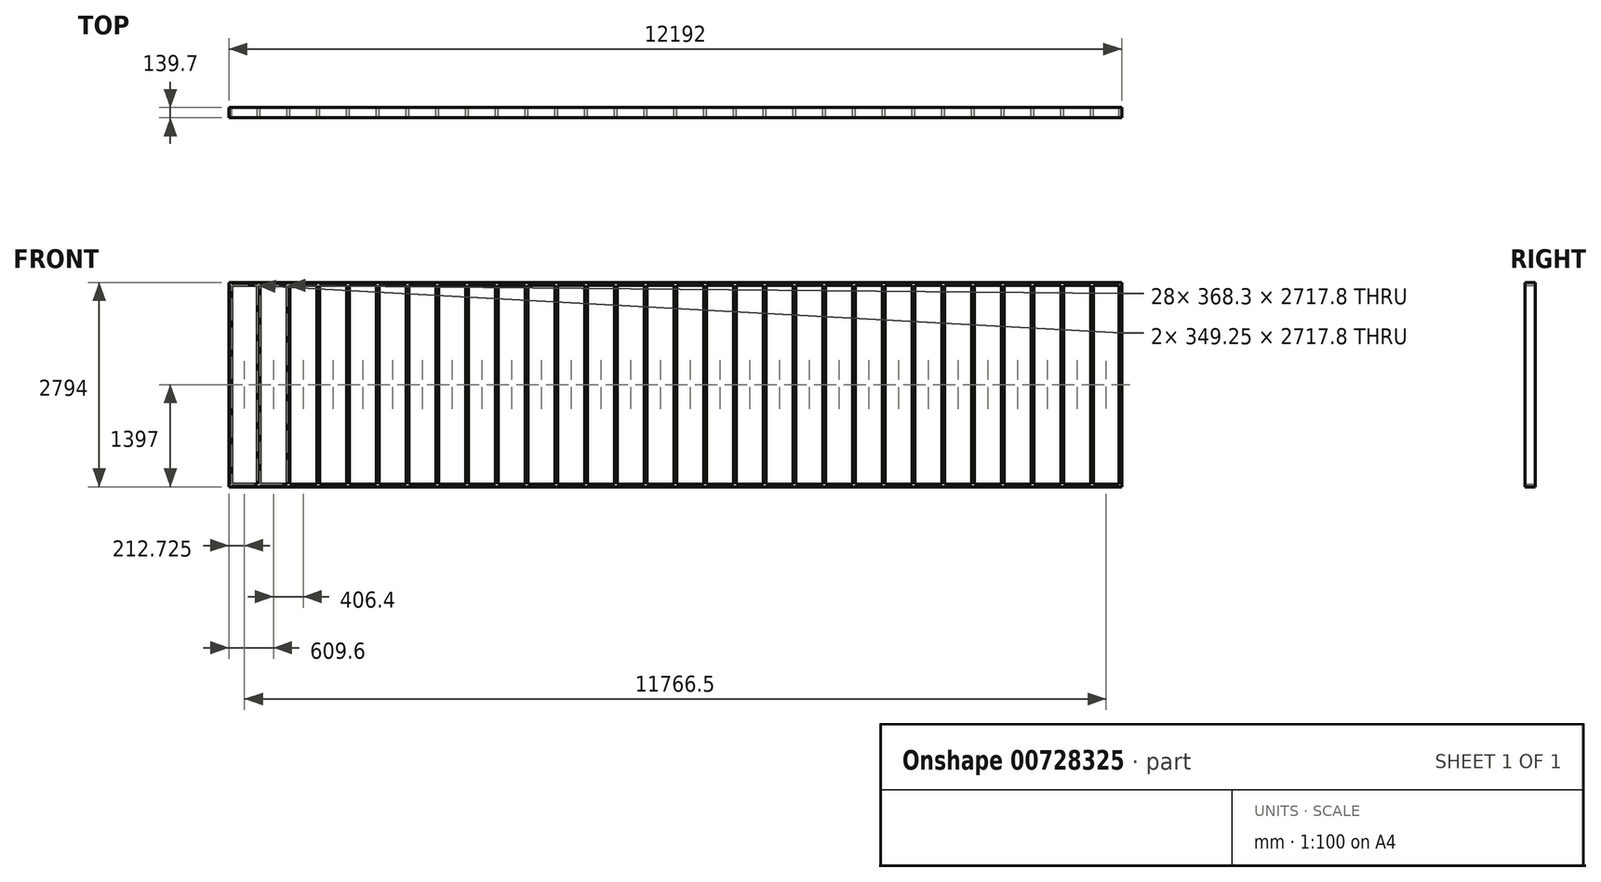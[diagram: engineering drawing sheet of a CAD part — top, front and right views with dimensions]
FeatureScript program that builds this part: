
annotation { "Feature Type Name" : "Feature", "Feature Type Description" : "" }
export const myFeature = defineFeature(function(context is Context, id is Id, definition is map)
    precondition{}
    {
        {
            var Q0;
            Q0=qCreatedBy(makeId("Front.planeOp"),FACE);
            var sketch = newSketch(context, id + "F0", { "sketchPlane" : qUnion([Q0])});
            skLineSegment(sketch, "E0.bottom", {"start": v(-6096, -1397) * mm, "end": v(6096, -1397) * mm});
            skLineSegment(sketch, "E0.top", {"start": v(-6096, 1397) * mm, "end": v(6096, 1397) * mm});
            skLineSegment(sketch, "E0.left", {"start": v(-6096, -1397) * mm, "end": v(-6096, 1397) * mm});
            skLineSegment(sketch, "E0.right", {"start": v(6096, -1397) * mm, "end": v(6096, 1397) * mm});
            skPoint(sketch, "E0.middle", {"position": v(0, 0) * mm});
            skLineSegment(sketch, "E1.0", {"start": v(-6057.9, -1358.9) * mm, "end": v(-6057.9, 1358.9) * mm});
            skLineSegment(sketch, "E2.0", {"start": v(-5708.65, -1358.9) * mm, "end": v(-5708.65, 1358.9) * mm});
            skLineSegment(sketch, "E3.0", {"start": v(-5670.55, -1358.9) * mm, "end": v(-5670.55, 1358.9) * mm});
            skLineSegment(sketch, "E4.0", {"start": v(-5302.25, -1358.9) * mm, "end": v(-5302.25, 1358.9) * mm});
            skLineSegment(sketch, "E5.0", {"start": v(-5264.15, -1358.9) * mm, "end": v(-5264.15, 1358.9) * mm});
            skLineSegment(sketch, "E6.0", {"start": v(-4895.85, -1358.9) * mm, "end": v(-4895.85, 1358.9) * mm});
            skLineSegment(sketch, "E7.0", {"start": v(-4857.75, -1358.9) * mm, "end": v(-4857.75, 1358.9) * mm});
            skLineSegment(sketch, "E8.0", {"start": v(-4489.45, -1358.9) * mm, "end": v(-4489.45, 1358.9) * mm});
            skLineSegment(sketch, "E9.0", {"start": v(-4451.35, -1358.9) * mm, "end": v(-4451.35, 1358.9) * mm});
            skLineSegment(sketch, "E10.0", {"start": v(-4083.05, -1358.9) * mm, "end": v(-4083.05, 1358.9) * mm});
            skLineSegment(sketch, "E11.0", {"start": v(-4044.95, -1358.9) * mm, "end": v(-4044.95, 1358.9) * mm});
            skLineSegment(sketch, "E12.0", {"start": v(-3676.65, -1358.9) * mm, "end": v(-3676.65, 1358.9) * mm});
            skLineSegment(sketch, "E13.0", {"start": v(-3638.55, -1358.9) * mm, "end": v(-3638.55, 1358.9) * mm});
            skLineSegment(sketch, "E14.0", {"start": v(-3270.25, -1358.9) * mm, "end": v(-3270.25, 1358.9) * mm});
            skLineSegment(sketch, "E15.0", {"start": v(-3232.15, -1358.9) * mm, "end": v(-3232.15, 1358.9) * mm});
            skLineSegment(sketch, "E16.0", {"start": v(-2863.85, -1397) * mm, "end": v(-2863.85, 1358.9) * mm});
            skLineSegment(sketch, "E17.0", {"start": v(-2825.75, -1397) * mm, "end": v(-2825.75, 1358.9) * mm});
            skLineSegment(sketch, "E18.0", {"start": v(-2457.45, -1358.9) * mm, "end": v(-2457.45, 1358.9) * mm});
            skLineSegment(sketch, "E19.0", {"start": v(-2419.35, -1358.9) * mm, "end": v(-2419.35, 1358.9) * mm});
            skLineSegment(sketch, "E20.0", {"start": v(-2051.05, -1358.9) * mm, "end": v(-2051.05, 1358.9) * mm});
            skLineSegment(sketch, "E21.0", {"start": v(-2012.95, -1358.9) * mm, "end": v(-2012.95, 1358.9) * mm});
            skLineSegment(sketch, "E22.0", {"start": v(-1644.65, -1358.9) * mm, "end": v(-1644.65, 1358.9) * mm});
            skLineSegment(sketch, "E23.0", {"start": v(-1606.55, -1358.9) * mm, "end": v(-1606.55, 1358.9) * mm});
            skLineSegment(sketch, "E24.0", {"start": v(-1238.25, -1358.9) * mm, "end": v(-1238.25, 1358.9) * mm});
            skLineSegment(sketch, "E25.0", {"start": v(-1200.15, -1358.9) * mm, "end": v(-1200.15, 1358.9) * mm});
            skLineSegment(sketch, "E26.0", {"start": v(-831.85, -1358.9) * mm, "end": v(-831.85, 1358.9) * mm});
            skLineSegment(sketch, "E27.0", {"start": v(-793.75, -1358.9) * mm, "end": v(-793.75, 1358.9) * mm});
            skLineSegment(sketch, "E28.0", {"start": v(-425.45, -1358.9) * mm, "end": v(-425.45, 1358.9) * mm});
            skLineSegment(sketch, "E29.0", {"start": v(-387.35, -1358.9) * mm, "end": v(-387.35, 1358.9) * mm});
            skLineSegment(sketch, "E30.0", {"start": v(-19.05, -1358.9) * mm, "end": v(-19.05, 1358.9) * mm});
            skLineSegment(sketch, "E31.0", {"start": v(19.05, -1358.9) * mm, "end": v(19.05, 1358.9) * mm});
            skLineSegment(sketch, "E32.0", {"start": v(387.35, -1358.9) * mm, "end": v(387.35, 1358.9) * mm});
            skLineSegment(sketch, "E33.0", {"start": v(425.45, -1358.9) * mm, "end": v(425.45, 1358.9) * mm});
            skLineSegment(sketch, "E34.0", {"start": v(793.75, -1358.9) * mm, "end": v(793.75, 1358.9) * mm});
            skLineSegment(sketch, "E35.0", {"start": v(831.85, -1358.9) * mm, "end": v(831.85, 1358.9) * mm});
            skLineSegment(sketch, "E36.0", {"start": v(1200.15, -1358.9) * mm, "end": v(1200.15, 1358.9) * mm});
            skLineSegment(sketch, "E37.0", {"start": v(1238.25, -1358.9) * mm, "end": v(1238.25, 1358.9) * mm});
            skLineSegment(sketch, "E38.0", {"start": v(1606.55, -1358.9) * mm, "end": v(1606.55, 1358.9) * mm});
            skLineSegment(sketch, "E39.0", {"start": v(1644.65, -1358.9) * mm, "end": v(1644.65, 1358.9) * mm});
            skLineSegment(sketch, "E40.0", {"start": v(2012.95, -1358.9) * mm, "end": v(2012.95, 1358.9) * mm});
            skLineSegment(sketch, "E41.0", {"start": v(2051.05, -1358.9) * mm, "end": v(2051.05, 1358.9) * mm});
            skLineSegment(sketch, "E42.0", {"start": v(2419.35, -1358.9) * mm, "end": v(2419.35, 1358.9) * mm});
            skLineSegment(sketch, "E43.0", {"start": v(2457.45, -1358.9) * mm, "end": v(2457.45, 1358.9) * mm});
            skLineSegment(sketch, "E44.0", {"start": v(2825.75, -1358.9) * mm, "end": v(2825.75, 1358.9) * mm});
            skLineSegment(sketch, "E45.0", {"start": v(2863.85, -1358.9) * mm, "end": v(2863.85, 1358.9) * mm});
            skLineSegment(sketch, "E46.0", {"start": v(3232.15, -1358.9) * mm, "end": v(3232.15, 1358.9) * mm});
            skLineSegment(sketch, "E47.0", {"start": v(3270.25, -1358.9) * mm, "end": v(3270.25, 1358.9) * mm});
            skLineSegment(sketch, "E48.0", {"start": v(3638.55, -1358.9) * mm, "end": v(3638.55, 1358.9) * mm});
            skLineSegment(sketch, "E49.0", {"start": v(3676.65, -1358.9) * mm, "end": v(3676.65, 1358.9) * mm});
            skLineSegment(sketch, "E50.0", {"start": v(4044.95, -1358.9) * mm, "end": v(4044.95, 1358.9) * mm});
            skLineSegment(sketch, "E51.0", {"start": v(4083.05, -1358.9) * mm, "end": v(4083.05, 1358.9) * mm});
            skLineSegment(sketch, "E52.0", {"start": v(4451.35, -1358.9) * mm, "end": v(4451.35, 1358.9) * mm});
            skLineSegment(sketch, "E53.0", {"start": v(4489.45, -1358.9) * mm, "end": v(4489.45, 1358.9) * mm});
            skLineSegment(sketch, "E54.0", {"start": v(4857.75, -1358.9) * mm, "end": v(4857.75, 1358.9) * mm});
            skLineSegment(sketch, "E55.0", {"start": v(4895.85, -1358.9) * mm, "end": v(4895.85, 1358.9) * mm});
            skLineSegment(sketch, "E56.0", {"start": v(5264.15, -1358.9) * mm, "end": v(5264.15, 1358.9) * mm});
            skLineSegment(sketch, "E57.0", {"start": v(5302.25, -1358.9) * mm, "end": v(5302.25, 1358.9) * mm});
            skLineSegment(sketch, "E58.0", {"start": v(5670.55, -1358.9) * mm, "end": v(5670.55, 1358.9) * mm});
            skLineSegment(sketch, "E59.0", {"start": v(5708.65, -1358.9) * mm, "end": v(5708.65, 1358.9) * mm});
            skLineSegment(sketch, "E60.0", {"start": v(6057.9, -1358.9) * mm, "end": v(6057.9, 1358.9) * mm});
            skLineSegment(sketch, "E61.0", {"start": v(-6057.9, 1358.9) * mm, "end": v(-5708.65, 1358.9) * mm});
            skLineSegment(sketch, "E62.0", {"start": v(-6057.9, -1358.9) * mm, "end": v(-5708.65, -1358.9) * mm});
            skLineSegment(sketch, "E63.trimOffspring", {"start": v(-5264.15, 1358.9) * mm, "end": v(-4895.85, 1358.9) * mm});
            skLineSegment(sketch, "E64.trimOffspring", {"start": v(-5670.55, 1358.9) * mm, "end": v(-5302.25, 1358.9) * mm});
            skLineSegment(sketch, "E65.trimOffspring", {"start": v(-4857.75, 1358.9) * mm, "end": v(-4489.45, 1358.9) * mm});
            skLineSegment(sketch, "E66.trimOffspring", {"start": v(-4451.35, 1358.9) * mm, "end": v(-4083.05, 1358.9) * mm});
            skLineSegment(sketch, "E67.trimOffspring", {"start": v(-4044.95, 1358.9) * mm, "end": v(-3676.65, 1358.9) * mm});
            skLineSegment(sketch, "E68.trimOffspring", {"start": v(-3232.15, 1358.9) * mm, "end": v(-2863.85, 1358.9) * mm});
            skLineSegment(sketch, "E69.trimOffspring", {"start": v(-3638.55, 1358.9) * mm, "end": v(-3270.25, 1358.9) * mm});
            skLineSegment(sketch, "E70.trimOffspring", {"start": v(-2825.75, 1358.9) * mm, "end": v(-2457.45, 1358.9) * mm});
            skLineSegment(sketch, "E71.trimOffspring", {"start": v(-2419.35, 1358.9) * mm, "end": v(-2051.05, 1358.9) * mm});
            skLineSegment(sketch, "E72.trimOffspring", {"start": v(-2012.95, 1358.9) * mm, "end": v(-1644.65, 1358.9) * mm});
            skLineSegment(sketch, "E73.trimOffspring", {"start": v(-1606.55, 1358.9) * mm, "end": v(-1238.25, 1358.9) * mm});
            skLineSegment(sketch, "E74.trimOffspring", {"start": v(-1200.15, 1358.9) * mm, "end": v(-831.85, 1358.9) * mm});
            skLineSegment(sketch, "E75.trimOffspring", {"start": v(-793.75, 1358.9) * mm, "end": v(-425.45, 1358.9) * mm});
            skLineSegment(sketch, "E76.trimOffspring", {"start": v(-387.35, 1358.9) * mm, "end": v(-19.05, 1358.9) * mm});
            skLineSegment(sketch, "E77.trimOffspring", {"start": v(19.05, 1358.9) * mm, "end": v(387.35, 1358.9) * mm});
            skLineSegment(sketch, "E78.trimOffspring", {"start": v(425.45, 1358.9) * mm, "end": v(793.75, 1358.9) * mm});
            skLineSegment(sketch, "E79.trimOffspring", {"start": v(831.85, 1358.9) * mm, "end": v(1200.15, 1358.9) * mm});
            skLineSegment(sketch, "E80.trimOffspring", {"start": v(1238.25, 1358.9) * mm, "end": v(1606.55, 1358.9) * mm});
            skLineSegment(sketch, "E81.trimOffspring", {"start": v(1644.65, 1358.9) * mm, "end": v(2012.95, 1358.9) * mm});
            skLineSegment(sketch, "E82.trimOffspring", {"start": v(2051.05, 1358.9) * mm, "end": v(2419.35, 1358.9) * mm});
            skLineSegment(sketch, "E83.trimOffspring", {"start": v(2457.45, 1358.9) * mm, "end": v(2825.75, 1358.9) * mm});
            skLineSegment(sketch, "E84.trimOffspring", {"start": v(2863.85, 1358.9) * mm, "end": v(3232.15, 1358.9) * mm});
            skLineSegment(sketch, "E85.trimOffspring", {"start": v(3270.25, 1358.9) * mm, "end": v(3638.55, 1358.9) * mm});
            skLineSegment(sketch, "E86.trimOffspring", {"start": v(3676.65, 1358.9) * mm, "end": v(4044.95, 1358.9) * mm});
            skLineSegment(sketch, "E87.trimOffspring", {"start": v(4083.05, 1358.9) * mm, "end": v(4451.35, 1358.9) * mm});
            skLineSegment(sketch, "E88.trimOffspring", {"start": v(4489.45, 1358.9) * mm, "end": v(4857.75, 1358.9) * mm});
            skLineSegment(sketch, "E89.trimOffspring", {"start": v(4895.85, 1358.9) * mm, "end": v(5264.15, 1358.9) * mm});
            skLineSegment(sketch, "E90.trimOffspring", {"start": v(5302.25, 1358.9) * mm, "end": v(5670.55, 1358.9) * mm});
            skLineSegment(sketch, "E91.trimOffspring", {"start": v(5708.65, 1358.9) * mm, "end": v(6057.9, 1358.9) * mm});
            skLineSegment(sketch, "E92.trimOffspring", {"start": v(5708.65, -1358.9) * mm, "end": v(6057.9, -1358.9) * mm});
            skLineSegment(sketch, "E93.trimOffspring", {"start": v(5302.25, -1358.9) * mm, "end": v(5670.55, -1358.9) * mm});
            skLineSegment(sketch, "E94.trimOffspring", {"start": v(4895.85, -1358.9) * mm, "end": v(5264.15, -1358.9) * mm});
            skLineSegment(sketch, "E95.trimOffspring", {"start": v(4489.45, -1358.9) * mm, "end": v(4857.75, -1358.9) * mm});
            skLineSegment(sketch, "E96.trimOffspring", {"start": v(4083.05, -1358.9) * mm, "end": v(4451.35, -1358.9) * mm});
            skLineSegment(sketch, "E97.trimOffspring", {"start": v(3676.65, -1358.9) * mm, "end": v(4044.95, -1358.9) * mm});
            skLineSegment(sketch, "E98.trimOffspring", {"start": v(3270.25, -1358.9) * mm, "end": v(3638.55, -1358.9) * mm});
            skLineSegment(sketch, "E99.trimOffspring", {"start": v(2863.85, -1358.9) * mm, "end": v(3232.15, -1358.9) * mm});
            skLineSegment(sketch, "E100.trimOffspring", {"start": v(2457.45, -1358.9) * mm, "end": v(2825.75, -1358.9) * mm});
            skLineSegment(sketch, "E101.trimOffspring", {"start": v(2051.05, -1358.9) * mm, "end": v(2419.35, -1358.9) * mm});
            skLineSegment(sketch, "E102.trimOffspring", {"start": v(1644.65, -1358.9) * mm, "end": v(2012.95, -1358.9) * mm});
            skLineSegment(sketch, "E103.trimOffspring", {"start": v(1238.25, -1358.9) * mm, "end": v(1606.55, -1358.9) * mm});
            skLineSegment(sketch, "E104.trimOffspring", {"start": v(831.85, -1358.9) * mm, "end": v(1200.15, -1358.9) * mm});
            skLineSegment(sketch, "E105.trimOffspring", {"start": v(425.45, -1358.9) * mm, "end": v(793.75, -1358.9) * mm});
            skLineSegment(sketch, "E106.trimOffspring", {"start": v(19.05, -1358.9) * mm, "end": v(387.35, -1358.9) * mm});
            skLineSegment(sketch, "E107.trimOffspring", {"start": v(-387.35, -1358.9) * mm, "end": v(-19.05, -1358.9) * mm});
            skLineSegment(sketch, "E108.trimOffspring", {"start": v(-793.75, -1358.9) * mm, "end": v(-425.45, -1358.9) * mm});
            skLineSegment(sketch, "E109.trimOffspring", {"start": v(-1606.55, -1358.9) * mm, "end": v(-831.85, -1358.9) * mm});
            skLineSegment(sketch, "E110.trimOffspring", {"start": v(-2012.95, -1358.9) * mm, "end": v(-1644.65, -1358.9) * mm});
            skLineSegment(sketch, "E111.trimOffspring", {"start": v(-2419.35, -1358.9) * mm, "end": v(-2051.05, -1358.9) * mm});
            skLineSegment(sketch, "E112.trimOffspring", {"start": v(-3232.15, -1358.9) * mm, "end": v(-2863.85, -1358.9) * mm});
            skLineSegment(sketch, "E113.trimOffspring", {"start": v(-2825.75, -1358.9) * mm, "end": v(-2457.45, -1358.9) * mm});
            skLineSegment(sketch, "E114.trimOffspring", {"start": v(-3638.55, -1358.9) * mm, "end": v(-3270.25, -1358.9) * mm});
            skLineSegment(sketch, "E115.trimOffspring", {"start": v(-4044.95, -1358.9) * mm, "end": v(-3676.65, -1358.9) * mm});
            skLineSegment(sketch, "E116.trimOffspring", {"start": v(-4451.35, -1358.9) * mm, "end": v(-4083.05, -1358.9) * mm});
            skLineSegment(sketch, "E117.trimOffspring", {"start": v(-4857.75, -1358.9) * mm, "end": v(-4489.45, -1358.9) * mm});
            skLineSegment(sketch, "E118.trimOffspring", {"start": v(-5264.15, -1358.9) * mm, "end": v(-4895.85, -1358.9) * mm});
            skLineSegment(sketch, "E119.trimOffspring", {"start": v(-5670.55, -1358.9) * mm, "end": v(-5302.25, -1358.9) * mm});
            skSolve(sketch);
        }
        {
            var Q0;
            Q0=qSketchRegion(id+"F0",true);
            extrude(context, id + "F1", {"entities" : qUnion([Q0]), "depth" : 139.7 * mm});
        }
    });
